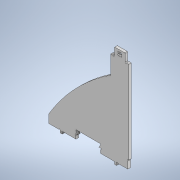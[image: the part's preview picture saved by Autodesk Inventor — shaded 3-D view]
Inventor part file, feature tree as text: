
AUTODESK INVENTOR PART (.ipt)
format: ipt  version: 2020 (Build 240168000, 168)  size: 380,416 bytes
history: native  units: mm
features: reference x2, other x2, extrude x1, sketch x1
ambient origin geometry x8: Origin, YZ Plane, XZ Plane, XY Plane, X Axis, Y Axis, Z Axis, Center Point
bodies: Body1 (feature_tree)
feature tree (6):
  extrude  "Extrusion4"  Depth=1.75mm
  sketch  "Sketch1"  dims[d13=550.0mm d19=150.0mm d54=220.0mm d56=220.0mm d57=30.0mm d59=30.0mm d73=236.680872mm d74=236.680872mm d75=576.435mm d76=472.393783mm d77=472.393783mm d78=30.0mm d82=252.393783mm d85=356.435mm d88=3.5mm d89=30.0mm d90=22.0mm d91=3.5mm d103=3.75mm d104=3.75mm d134=3.5mm d135=65.0mm d136=65.0mm d137=7.333333mm d138=60.0deg d139=5.0mm d140=7.5mm d148=1.75mm d151=40.0mm d152=74.50599mm d153=20.666667mm d154=3.5mm d155=189.01198mm d159=1.75mm d160=1.75mm d161=1.75mm d164=7.5mm d168=21.25mm d170=30.0mm d171=1.75mm d172=10.0mm d173=3.5mm d177=3.5mm d178=65.0mm d179=65.0mm d180=7.333333mm d181=60.0deg d182=5.0mm d183=7.5mm d184=30.0mm d185=1.75mm d186=10.0mm d192=1.75mm d206=1.75mm d208=220.0mm d209=3.5mm d210=65.0mm d211=65.0mm d212=7.333333mm d213=60.0deg d214=5.0mm d215=7.5mm d216=30.0mm d217=1.75mm d218=10.0mm d219=7.0mm d220=1.75mm d222=23.0mm d226=1.75mm d228=53.623497mm d231=1.75mm d232=1.75mm d233=7.0mm d234=1.75mm d235=23.0mm d236=1.75mm d237=252.393783mm d240=3.0mm d241=3.5mm d242=8.0mm d243=1.75mm d244=1.75mm d245=7.0mm d246=1.75mm d247=23.0mm d248=1.75mm d250=3.5mm d251=65.0mm d252=65.0mm d253=7.333333mm d254=60.0deg d255=5.0mm d256=7.5mm d257=30.0mm d258=1.75mm d259=10.0mm d260=53.623497mm d261=3.0mm d262=3.5mm d265=1.75mm d266=1.75mm d267=7.0mm d268=1.75mm d269=23.0mm d270=1.75mm d271=3.5mm d272=7.0mm d273=0.0mm d275=3.5mm d276=30.0mm d278=3.5mm d279=1.75mm d282=3.75mm d283=3.75mm d286=5.25mm d287=10.0mm d289=2.0mm d290=22.0mm d291=1.75mm d292=1.75mm d293=1.75mm]
  reference  "Reference1"
  reference  "Reference2"
  other  "Vertical Support Assembly.iam"
  other  "Support A - V2:1"
